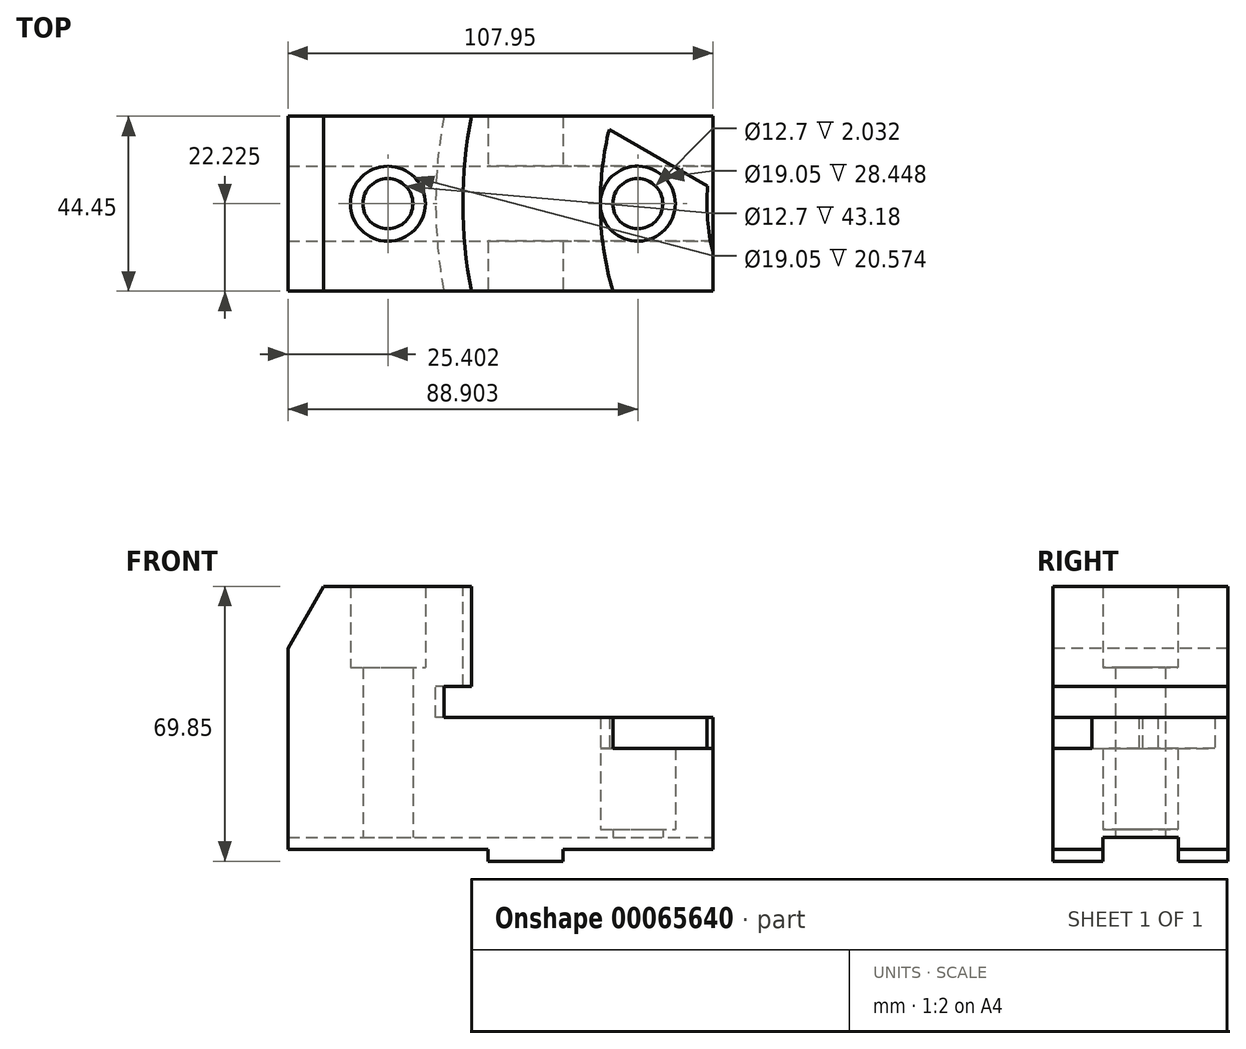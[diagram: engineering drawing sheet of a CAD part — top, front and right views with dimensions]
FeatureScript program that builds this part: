
annotation { "Feature Type Name" : "Feature", "Feature Type Description" : "" }
export const myFeature = defineFeature(function(context is Context, id is Id, definition is map)
    precondition{}
    {
        {
            var Q0;
            Q0=qCreatedBy(makeId("Front.planeOp"),FACE);
            var sketch = newSketch(context, id + "F0", { "sketchPlane" : qUnion([Q0])});
            skLineSegment(sketch, "E0.bottom", {"start": v(-53, 44.63) * mm, "end": v(54.94, 44.63) * mm});
            skLineSegment(sketch, "E0.top", {"start": v(-53, -25.22) * mm, "end": v(54.94, -25.22) * mm});
            skLineSegment(sketch, "E0.left", {"start": v(-53, 44.63) * mm, "end": v(-53, -25.22) * mm});
            skLineSegment(sketch, "E0.right", {"start": v(54.94, 44.63) * mm, "end": v(54.94, -25.22) * mm});
            skSolve(sketch);
        }
        {
            var Q0;
            Q0=makeQuery(id+"F0.imprint","IMPRINT",FACE,{"disambiguationData":[TD([[makeQuery(id+"F0.imprint","IMPRINT",EDGE,{"derivedFrom":sQuery(id+"F0.wireOp",EDGE,"E0.bottom")}),-1.0]])]});
            extrude(context, id + "F1", {"entities" : qUnion([Q0]), "depth" : 44.45 * mm});
        }
        {
            var Q0;
            Q0=makeQuery(id+"F1.opExtrude","CAP_FACE",FACE,{"disambiguationData":[OSD([sQuery(id+"F0.wireOp",EDGE,"E0.bottom"),sQuery(id+"F0.wireOp",EDGE,"E0.top"),sQuery(id+"F0.wireOp",EDGE,"E0.left"),sQuery(id+"F0.wireOp",EDGE,"E0.right")])],"isStart":false});
            var sketch = newSketch(context, id + "F2", { "sketchPlane" : qUnion([Q0])});
            skLineSegment(sketch, "E1.bottom", {"start": v(54.94, -25.22) * mm, "end": v(16.84, -25.22) * mm});
            skLineSegment(sketch, "E1.top", {"start": v(54.94, -22.18) * mm, "end": v(16.84, -22.18) * mm});
            skLineSegment(sketch, "E1.left", {"start": v(54.94, -25.22) * mm, "end": v(54.94, -22.18) * mm});
            skLineSegment(sketch, "E1.right", {"start": v(16.84, -25.22) * mm, "end": v(16.84, -22.18) * mm});
            skLineSegment(sketch, "E2.bottom", {"start": v(-53, -25.22) * mm, "end": v(-2.18, -25.22) * mm});
            skLineSegment(sketch, "E2.top", {"start": v(-53, -22.18) * mm, "end": v(-2.18, -22.18) * mm});
            skLineSegment(sketch, "E2.left", {"start": v(-53, -25.22) * mm, "end": v(-53, -22.18) * mm});
            skLineSegment(sketch, "E2.right", {"start": v(-2.18, -25.22) * mm, "end": v(-2.18, -22.18) * mm});
            skLineSegment(sketch, "E3", {"start": v(-53, 28.88) * mm, "end": v(-43.92, 44.63) * mm});
            skLineSegment(sketch, "E4", {"start": v(-43.92, 44.63) * mm, "end": v(-53, 49.87) * mm});
            skLineSegment(sketch, "E5", {"start": v(-53, 49.87) * mm, "end": v(-64.47, 30.03) * mm});
            skLineSegment(sketch, "E6", {"start": v(-64.47, 30.03) * mm, "end": v(-53, 28.88) * mm});
            skSolve(sketch);
        }
        {
            var Q0;
            Q0=makeQuery(id+"F2.imprint","IMPRINT",FACE,{"disambiguationData":[TD([[makeQuery(id+"F2.imprint","IMPRINT",EDGE,{"derivedFrom":sQuery(id+"F2.wireOp",EDGE,"E2.bottom")}),1.0]])]});
            var Q1;
            Q1=makeQuery(id+"F2.imprint","IMPRINT",FACE,{"disambiguationData":[TD([[makeQuery(id+"F2.imprint","IMPRINT",EDGE,{"derivedFrom":sQuery(id+"F2.wireOp",EDGE,"E1.bottom")}),1.0]])]});
            var Q2;
            {var subQ3=sQuery(id+"F2.wireOp",EDGE,"E4");Q2=makeQuery(id+"F2.imprint","IMPRINT",FACE,{"disambiguationData":[TD([[makeQuery(id+"F2.imprint","IMPRINT",EDGE,{"derivedFrom":subQ3}),1.0]])]});}
            var Q3;
            {var subQ0=sQuery(id+"F2.wireOp",EDGE,"E3");Q3=makeQuery(id+"F2.imprint","IMPRINT",FACE,{"disambiguationData":[TD([[makeQuery(id+"F2.imprint","IMPRINT",EDGE,{"derivedFrom":subQ0}),1.0]])]});}
            extrude(context, id + "F3", {"entities" : qUnion([Q0, Q1, Q2, Q3]), "operationType" : NewBodyOperationType.REMOVE, "oppositeDirection" : true, "depth" : 66.64 * mm, "hasSecondDirection" : true, "secondDirectionBound" : BoundingType.THROUGH_ALL, "secondDirectionOppositeDirection" : false, "secondDirectionDepth" : 25.4 * mm});
        }
        {
            var Q0;
            Q0=makeQuery(id+"F1.opExtrude","SWEPT_FACE",FACE,{"disambiguationData":[OSD([sQuery(id+"F0.wireOp",EDGE,"E0.right")])]});
            var sketch = newSketch(context, id + "F4", { "sketchPlane" : qUnion([Q0])});
            skLineSegment(sketch, "E7.bottom", {"start": v(-31.75, -39.28) * mm, "end": v(-12.65, -39.28) * mm});
            skLineSegment(sketch, "E7.top", {"start": v(-31.75, -19.13) * mm, "end": v(-12.65, -19.13) * mm});
            skLineSegment(sketch, "E7.left", {"start": v(-31.75, -39.28) * mm, "end": v(-31.75, -19.13) * mm});
            skLineSegment(sketch, "E7.right", {"start": v(-12.65, -39.28) * mm, "end": v(-12.65, -19.13) * mm});
            skSolve(sketch);
        }
        {
            var Q0;
            {var subQ0=sQuery(id+"F4.wireOp",EDGE,"E7.top");Q0=makeQuery(id+"F4.imprint","IMPRINT",FACE,{"disambiguationData":[TD([[makeQuery(id+"F4.imprint","IMPRINT",EDGE,{"derivedFrom":subQ0}),-1.0]])]});}
            var Q1;
            {var subQ0=sQuery(id+"F4.wireOp",EDGE,"E7.bottom");Q1=makeQuery(id+"F4.imprint","IMPRINT",FACE,{"disambiguationData":[TD([[makeQuery(id+"F4.imprint","IMPRINT",EDGE,{"derivedFrom":subQ0}),1.0]])]});}
            extrude(context, id + "F5", {"entities" : qUnion([Q0, Q1]), "operationType" : NewBodyOperationType.REMOVE, "endBound" : BoundingType.THROUGH_ALL, "oppositeDirection" : true, "depth" : 25.4 * mm});
        }
        {
            var Q0;
            Q0=makeQuery(id+"F1.opExtrude","SWEPT_FACE",FACE,{"disambiguationData":[OSD([sQuery(id+"F0.wireOp",EDGE,"E0.bottom")])]});
            var sketch = newSketch(context, id + "F6", { "sketchPlane" : qUnion([Q0])});
            skLineSegment(sketch, "E8", {"start": v(-8.56, -44.45) * mm, "end": v(-8.56, 0) * mm, "construction": true});
            skLineSegment(sketch, "E9", {"start": v(-8.56, -22.23) * mm, "end": v(105.74, -22.22) * mm, "construction": true});
            skPoint(sketch, "E9.endSnap0", {"position": v(54.94, -22.23) * mm});
            skArc(sketch, "E10", {"start": v(-0.84, 19.07) * mm, "mid": v(-8.54, -24.4) * mm, "end": v(0.81, -67.55) * mm});
            skLineSegment(sketch, "E11", {"start": v(105.74, -22.22) * mm, "end": v(84.23, 4.74) * mm});
            skLineSegment(sketch, "E12", {"start": v(84.23, 4.74) * mm, "end": v(-0.84, 19.07) * mm});
            skLineSegment(sketch, "E13", {"start": v(105.74, -22.23) * mm, "end": v(81.33, -56.9) * mm});
            skLineSegment(sketch, "E14", {"start": v(81.33, -56.9) * mm, "end": v(0.81, -67.55) * mm});
            skSolve(sketch);
        }
        {
            var Q0;
            Q0 = qSketchRegion(id + "F6", true);
            extrude(context, id + "F7", {"entities" : qUnion([Q0]), "operationType" : NewBodyOperationType.REMOVE, "oppositeDirection" : true, "depth" : 33.27 * mm});
        }
        {
            var Q0;
            Q0=makeQuery(id+"F1.opExtrude","CAP_FACE",FACE,{"disambiguationData":[OSD([sQuery(id+"F0.wireOp",EDGE,"E0.bottom"),sQuery(id+"F0.wireOp",EDGE,"E0.top"),sQuery(id+"F0.wireOp",EDGE,"E0.left"),sQuery(id+"F0.wireOp",EDGE,"E0.right")])],"isStart":false});
            cPlane(context, id + "F8", {"entities" : qUnion([Q0]), "cplaneType" : CPlaneType.OFFSET, "offset" : 1.75 / 50.8 * mm, "oppositeDirection" : true, "width" : 152.4 * mm, "height" : 152.4 * mm});
        }
        {
            var Q0;
            Q0=qCreatedBy(id+"F8.planeOp",FACE);
            var sketch = newSketch(context, id + "F9", { "sketchPlane" : qUnion([Q0])});
            skLineSegment(sketch, "E15.bottom", {"start": v(-13.38, 11.35) * mm, "end": v(5.58, 11.35) * mm});
            skLineSegment(sketch, "E15.top", {"start": v(-13.38, 19.23) * mm, "end": v(5.58, 19.23) * mm});
            skLineSegment(sketch, "E15.left", {"start": v(-13.38, 11.35) * mm, "end": v(-13.38, 19.23) * mm});
            skLineSegment(sketch, "E15.right", {"start": v(5.58, 11.35) * mm, "end": v(5.58, 19.23) * mm});
            skSolve(sketch);
        }
        {
            var Q0;
            Q0=makeQuery(id+"F9.imprint","IMPRINT",FACE,{"disambiguationData":[TD([[makeQuery(id+"F9.imprint","IMPRINT",EDGE,{"derivedFrom":sQuery(id+"F9.wireOp",EDGE,"E15.bottom")}),1.0]])]});
            var Q1;
            Q1=makeQuery(id+"F7.boolean.opBoolean","COPY",FACE,{"derivedFrom":makeQuery(id+"F7.opExtrude","SWEPT_FACE",FACE,{"disambiguationData":[OSD([sQuery(id+"F6.wireOp",EDGE,"E10")])]})});
            revolve(context, id + "F10", {"operationType" : NewBodyOperationType.REMOVE, "entities" : qUnion([Q0]), "axis" : qUnion([Q1]), "revolveType" : RevolveType.TWO_DIRECTIONS, "angle" : 30 * degree, "angleBack" : 30 * degree});
        }
        {
            var Q0;
            Q0=qCreatedBy(id+"F8.planeOp",FACE);
            var sketch = newSketch(context, id + "F11", { "sketchPlane" : qUnion([Q0])});
            skLineSegment(sketch, "E16.bottom", {"start": v(29.54, 17.88) * mm, "end": v(58.41, 17.88) * mm});
            skLineSegment(sketch, "E16.top", {"start": v(29.54, 3.48) * mm, "end": v(58.41, 3.48) * mm});
            skLineSegment(sketch, "E16.left", {"start": v(29.54, 17.88) * mm, "end": v(29.54, 3.48) * mm});
            skLineSegment(sketch, "E16.right", {"start": v(58.41, 17.88) * mm, "end": v(58.41, 3.48) * mm});
            skSolve(sketch);
        }
        {
            var Q0;
            Q0=makeQuery(id+"F11.imprint","IMPRINT",FACE,{"disambiguationData":[TD([[makeQuery(id+"F11.imprint","IMPRINT",EDGE,{"derivedFrom":sQuery(id+"F11.wireOp",EDGE,"E16.bottom")}),-1.0]])]});
            var Q1;
            Q1=makeQuery(id+"F7.boolean.opBoolean","COPY",FACE,{"derivedFrom":makeQuery(id+"F7.opExtrude","SWEPT_FACE",FACE,{"disambiguationData":[OSD([sQuery(id+"F6.wireOp",EDGE,"E10")])]})});
            revolve(context, id + "F12", {"operationType" : NewBodyOperationType.REMOVE, "entities" : qUnion([Q0]), "axis" : qUnion([Q1]), "revolveType" : RevolveType.SYMMETRIC, "oppositeDirection" : true, "angle" : 60 * degree});
        }
        {
            var Q0;
            Q0=makeQuery(id+"F1.opExtrude","SWEPT_FACE",FACE,{"disambiguationData":[OSD([sQuery(id+"F0.wireOp",EDGE,"E0.bottom")])]});
            var sketch = newSketch(context, id + "F13", { "sketchPlane" : qUnion([Q0])});
            skPoint(sketch, "E17", {"position": v(-27.6, -22.23) * mm});
            skSolve(sketch);
        }
        {
            var Q0;
            Q0=makeQuery(id+"F10.boolean.opBoolean","MERGE",FACE,{"derivedFrom":[makeQuery(id+"F7.boolean.opBoolean","COPY",FACE,{"derivedFrom":makeQuery(id+"F7.opExtrude","CAP_FACE",FACE,{"disambiguationData":[OSD([sQuery(id+"F6.wireOp",EDGE,"E10"),sQuery(id+"F6.wireOp",EDGE,"E11"),sQuery(id+"F6.wireOp",EDGE,"E12"),sQuery(id+"F6.wireOp",EDGE,"E13"),sQuery(id+"F6.wireOp",EDGE,"E14")])],"isStart":false})}),makeQuery(id+"F10.opRevolve","SWEPT_FACE",FACE,{"disambiguationData":[OSD([sQuery(id+"F9.wireOp",EDGE,"E15.bottom")])]})]});
            var sketch = newSketch(context, id + "F14", { "sketchPlane" : qUnion([Q0])});
            skPoint(sketch, "E18", {"position": v(35.9, -22.23) * mm});
            skSolve(sketch);
        }
        {
            var Q0;
            Q0=sQuery(id+"F13.wireOp",VERTEX,"E17");
            var Q1;
            Q1=sQuery(id+"F14.wireOp",VERTEX,"E18");
            var Q2;
            Q2=makeQuery(id+"F1.opExtrude","SWEPT_BODY",BODY,{"disambiguationData":[OSD([sQuery(id+"F0.wireOp",EDGE,"E0.bottom"),sQuery(id+"F0.wireOp",EDGE,"E0.top"),sQuery(id+"F0.wireOp",EDGE,"E0.left"),sQuery(id+"F0.wireOp",EDGE,"E0.right")])]});
            hole(context, id + "F15", {"style" : HoleStyle.C_BORE, "holeDiameter" : 12.7 * mm, "cBoreDiameter" : 19.05 * mm, "cBoreDepth" : 20.57 * mm, "endStyle" : HoleEndStyle.THROUGH, "locations" : qUnion([Q0, Q1]), "scope" : qUnion([Q2])});
        }
    });
